# Revit family: Ридан_Термостат защиты от замерзания KP61R
name_source: partatom
category: Арматура трубопроводов
units: mm (PartAtom-declared; Revit-internal decimal feet)

## family parameters
Всегда вертикально = Да
На основе рабочей плоскости = Нет
Общий = Нет
При загрузке вырезать с полостями = Нет
Размер круглого соединителя = Использовать диаметр
Тип детали = Нормальный

## types (4) — shared parameters
ADSK_Версия Revit = 2019
ADSK_Версия семейства = 1.0
ADSK_Единица измерения = шт.
ADSK_Завод-изготовитель = ООО «Ридан-Трейд»
ADSK_Количество = 1
ADSK_Марка = KP61R
ADSK_Масса = 0.5
LT = KPI61R

## per-type parameters (varying)
| type | A | ADSK_Код изделия | ADSK_Наименование |
| 060L126666R - 1 м | 1 мм | 060L126666R | Термостат защиты от замерзания KP61R,  капиллярная трубка 1 м |
| 060L126766R - 3 м | 2 мм | 060L126766R | Термостат защиты от замерзания KP61R,  капиллярная трубка 3 м |
| 060L126466R - 6 м | 3 мм | 060L126466R | Термостат защиты от замерзания KP61R,  капиллярная трубка 6 м |
| 060L126566R - 12 м | 4 мм | 060L126566R | Термостат защиты от замерзания KP61R,  капиллярная трубка 12 м |
